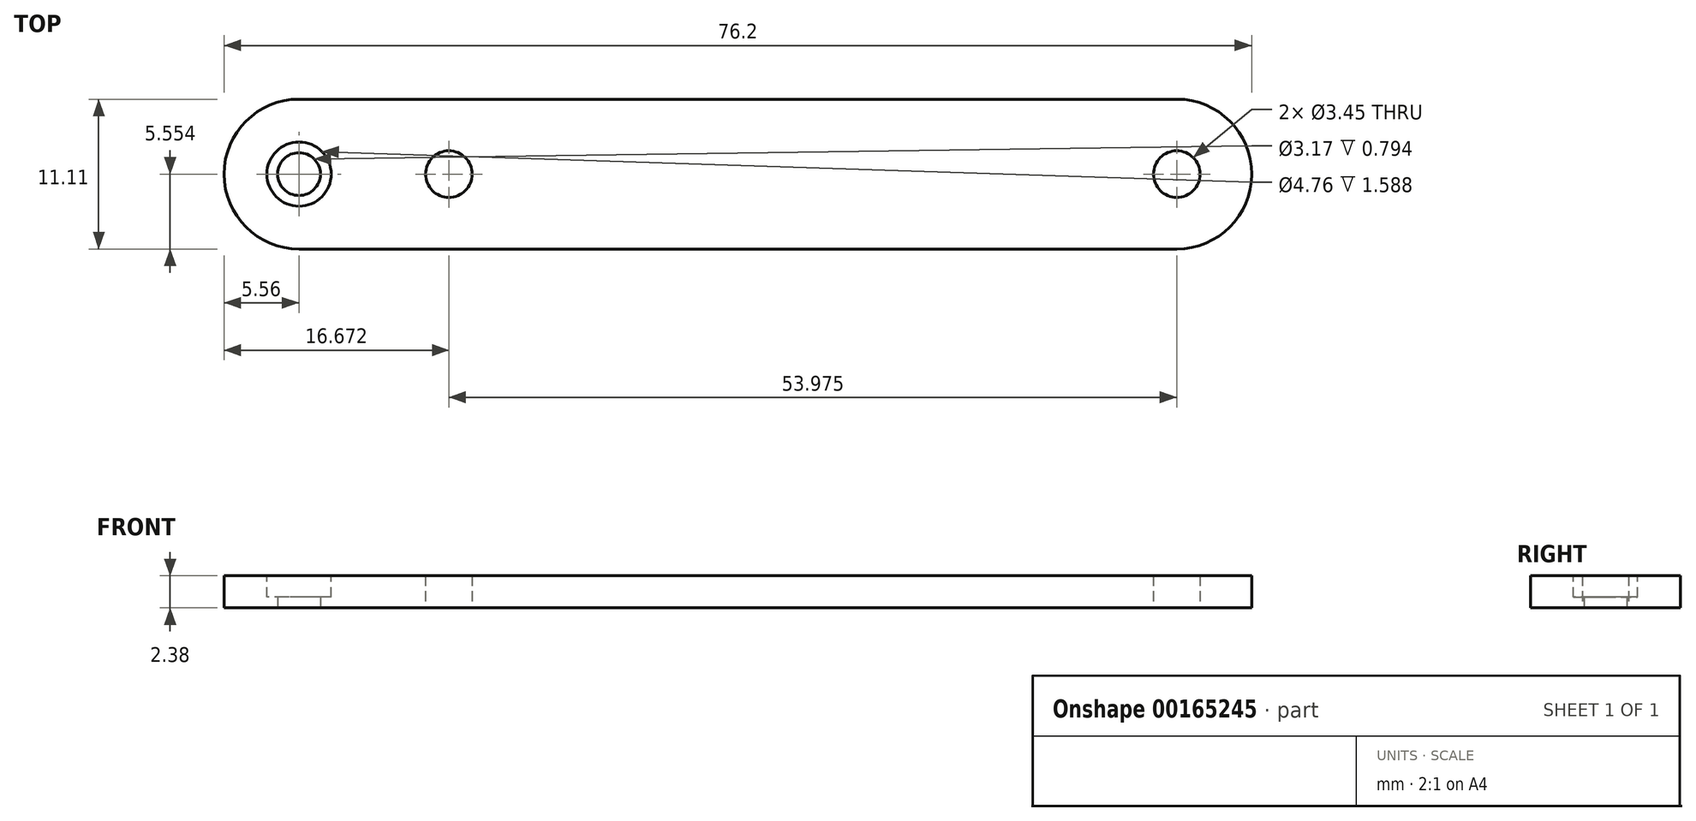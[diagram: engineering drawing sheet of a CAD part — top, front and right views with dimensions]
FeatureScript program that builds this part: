
annotation { "Feature Type Name" : "Feature", "Feature Type Description" : "" }
export const myFeature = defineFeature(function(context is Context, id is Id, definition is map)
    precondition{}
    {
        {
            var Q0;
            Q0=qCreatedBy(makeId("Top.planeOp"),FACE);
            var sketch = newSketch(context, id + "F0", { "sketchPlane" : qUnion([Q0])});
            skLineSegment(sketch, "E0.bottom", {"start": v(0, 0) * mm, "end": v(65.09, 0) * mm});
            skLineSegment(sketch, "E0.top", {"start": v(0, -11.11) * mm, "end": v(65.09, -11.11) * mm});
            skLineSegment(sketch, "E0.left", {"start": v(0, 0) * mm, "end": v(0, -11.11) * mm, "construction": true});
            skLineSegment(sketch, "E0.right", {"start": v(65.09, 0) * mm, "end": v(65.09, -11.11) * mm, "construction": true});
            skArc(sketch, "E1", {"start": v(0, 0) * mm, "mid": v(-5.56, -5.56) * mm, "end": v(0, -11.11) * mm});
            skCircle(sketch, "E2", {"center": v(0, -5.56) * mm, "radius": 1.59 * mm});
            skLineSegment(sketch, "E3", {"start": v(0, -5.56) * mm, "end": v(11.11, -5.56) * mm, "construction": true});
            skCircle(sketch, "E4", {"center": v(11.11, -5.56) * mm, "radius": 1.73 * mm});
            skCircle(sketch, "E5", {"center": v(65.09, -5.56) * mm, "radius": 1.73 * mm});
            skArc(sketch, "E6", {"start": v(65.09, -11.11) * mm, "mid": v(70.64, -5.56) * mm, "end": v(65.09, 0) * mm});
            skSolve(sketch);
        }
        {
            var Q0;
            {var subQ5=sQuery(id+"F0.wireOp",EDGE,"E0.bottom");Q0=makeQuery(id+"F0.imprint","IMPRINT",FACE,{"disambiguationData":[TD([[makeQuery(id+"F0.imprint","IMPRINT",EDGE,{"derivedFrom":subQ5}),-1.0]])]});}
            extrude(context, id + "F1", {"entities" : qUnion([Q0]), "depth" : 2.38 * mm});
        }
        {
            var Q0;
            Q0=makeQuery(id+"F1.opExtrude","CAP_FACE",FACE,{"disambiguationData":[OSD([sQuery(id+"F0.wireOp",EDGE,"E0.bottom"),sQuery(id+"F0.wireOp",EDGE,"E0.top"),sQuery(id+"F0.wireOp",EDGE,"E1"),sQuery(id+"F0.wireOp",EDGE,"E2"),sQuery(id+"F0.wireOp",EDGE,"E4"),sQuery(id+"F0.wireOp",EDGE,"E5"),sQuery(id+"F0.wireOp",EDGE,"E6")])],"isStart":false});
            var sketch = newSketch(context, id + "F2", { "sketchPlane" : qUnion([Q0])});
            skCircle(sketch, "E7", {"center": v(0, -5.56) * mm, "radius": 2.38 * mm});
            skSolve(sketch);
        }
        {
            var Q0;
            Q0 = qSketchRegion(id + "F2", true);
            extrude(context, id + "F3", {"entities" : qUnion([Q0]), "operationType" : NewBodyOperationType.REMOVE, "oppositeDirection" : true, "depth" : 1.59 * mm});
        }
    });
